# Revit family: R-MTD-300
name_source: partatom
category: Portes
revit_build: Autodesk Revit 2017 (Build: 20190508_0315(x64)
units: mm (PartAtom-declared; Revit-internal decimal feet)

## family parameters
Couper avec des vides une fois chargée = Non
Hôte = Mur
Partagée = Non
Point de calcul de pièce = Non
Toujours verticalement = Oui

## types (1)
- MTD-300
    1 Vantail = Oui
    2 Vantaux = Non
    Angle Rail 1 = 3.00°
    Angle Rail 2 = 3.00°
    Butée en L = Non
    Butée en U = Oui
    Certification = D.A.S. Mode 2 certifié NF
    Construction analytique = <Aucun>
    DAS = Oui
    DC Fixation_Rail = 150 mm  [stored 0.492126 ft]
    DC Jeu Avant = 0 mm  [stored 0 ft]
    DC Jeu Haut = 0 mm  [stored 0 ft]
    DC Portillon = 0 mm  [stored 0 ft]
    DC Profil Butée = 0 mm  [stored 0 ft]
    Description = Bloc-porte métal industriel D.A.S. M 611 SL - DAS porte coulissante de parking avec portillon va-et-vient posée sur linteau, E60, D.A.S. certifié NF, sur rail droit, avec guidage par sabots de sol, pour baie maxi 6000x2750
    Désax 2V Asymétrique = 0 mm  [stored 0 ft]
    Ep Butée = 178 mm  [stored 0.58399 ft]
    Ep Chicane Murale = 200 mm  [stored 0.656168 ft]
    Ep Face Coté Baie = 10 mm  [stored 0.0328084 ft]
    Ep Face Coté Opposé Baie = 10 mm  [stored 0.0328084 ft]
    Ep Fond Butée = 11 mm  [stored 0.0360892 ft]
    Ep Rail = 3 mm  [stored 0.00984252 ft]
    Ep Vantail = 82 mm  [stored 0.269029 ft]
    Fabricant = Malerba
    Fiche_Produit = MTD-300
    Fixation Linteau = Oui
    Fixation sous Dalle = Non
    Hauteur Baie = 2200 mm  [stored 7.21785 ft]
    Hauteur Profil Rail = 44 mm
    Hauteur sous Dalle = 3000 mm  [stored 9.84252 ft]
    Ht Fixation Linteau = 430 mm
    Ht Portillon = 2000 mm  [stored 6.56168 ft]
    Jeu Portillon Bas = 51 mm
    Jeu Portillon Coté Opposé Pivot = 10 mm  [stored 0.0328084 ft]
    Jeu Portillon Coté Pivot = 10 mm  [stored 0.0328084 ft]
    Jeu Portillon Haut = 10 mm  [stored 0.0328084 ft]
    Jeu Vantail Bas = 10 mm  [stored 0.0328084 ft]
    Larg Portillon = 900 mm  [stored 2.95276 ft]
    Larg Vantail Primaire Asymétrique = 2400 mm
    Largeur Baie = 3000 mm  [stored 9.84252 ft]
    Lgt Fix Vantail Primaire = 6325 mm  [stored 20.7513 ft]
    Lgt Fix Vantail Second = 6325 mm  [stored 20.7513 ft]
    Lgt Rail Second = 6825 mm  [stored 22.3917 ft]
    Mat Ame = Acier galvanisé
    Mat Quinc = <Par catégorie>
    Modèle = 16 - Coulissante
    Montage sur Mur Perpendiculaire = Non
    Note d'identification = 1V E60 - DAS COULISSANT DE PARKING + PORTILLON SUR LINTEAU
    Position Vantail Mur = 91 mm  [stored 0.298556 ft]
    Prof Butée = 260 mm  [stored 0.853018 ft]
    Prof Chicane Murale = 50 mm  [stored 0.164042 ft]
    Prof Coté Butée = 71 mm
    Profondeur Rail = 49 mm  [stored 0.160761 ft]
    Rec Arrière = 215 mm
    Rec Avant = 160 mm  [stored 0.524934 ft]
    Rec Haut = 200 mm  [stored 0.656168 ft]
    Reference_Commerciale = M 611 LS - DAS
    Resistance_Feu = E60
    Retours Rails = 17 mm
    Sens_Feu = Recto / Verso
    URL = https://www.malerba.fr
    Vantaux Asymétriques = Non
    lgt Rail Primaire = 6825 mm  [stored 22.3917 ft]
    temp = 0 mm  [stored 0 ft]

note: [stored X ft] marks values corroborated as IEEE doubles in the binary element streams (Revit-internal decimal feet)

## geometry (parser evidence)
native form markers: Blend x10
no freeform markers — native parametric forms only
